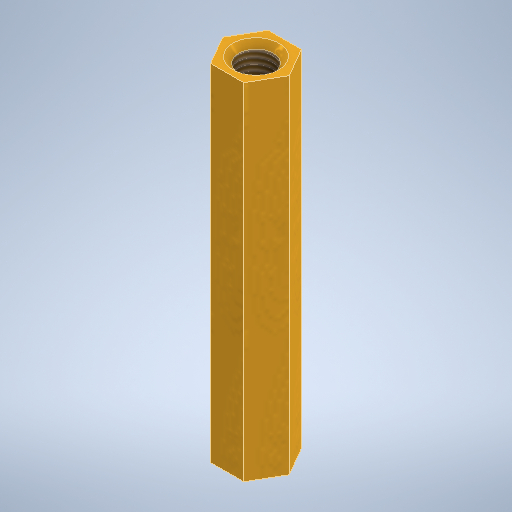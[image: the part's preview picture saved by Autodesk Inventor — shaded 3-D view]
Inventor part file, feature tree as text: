
AUTODESK INVENTOR PART (.ipt)
format: ipt  version: 2025.1 (Build 291241000, 241)  size: 279,040 bytes
history: native  units: mm
features: other x1, extrude x1, chamfer x1, thread x1, sketch x1
ambient origin geometry x8: Origin, YZ Plane, XZ Plane, XY Plane, X Axis, Y Axis, Z Axis, Center Point
bodies: Body1 (feature_tree)
feature tree (5):
  other  "Sólido1"
  extrude  "Extrusão1"  Depth=30.0mm TaperAngle=45.0deg
  chamfer  "Chanfro1"  Distance=29.0mm
  thread  "Rosca1"  [1 undecoded]
  sketch  "Esboço1"  dims[d2=30.0mm d3=0.0mm d4=0.5mm d5=2.0mm d6=45.0deg d7=29.0mm d8=0.0mm]
note: 1 required parameter value undecoded (feature->parameter linkage not recoverable at this tier; creation-order binding heuristic only, values carry confidence <= 0.55)
